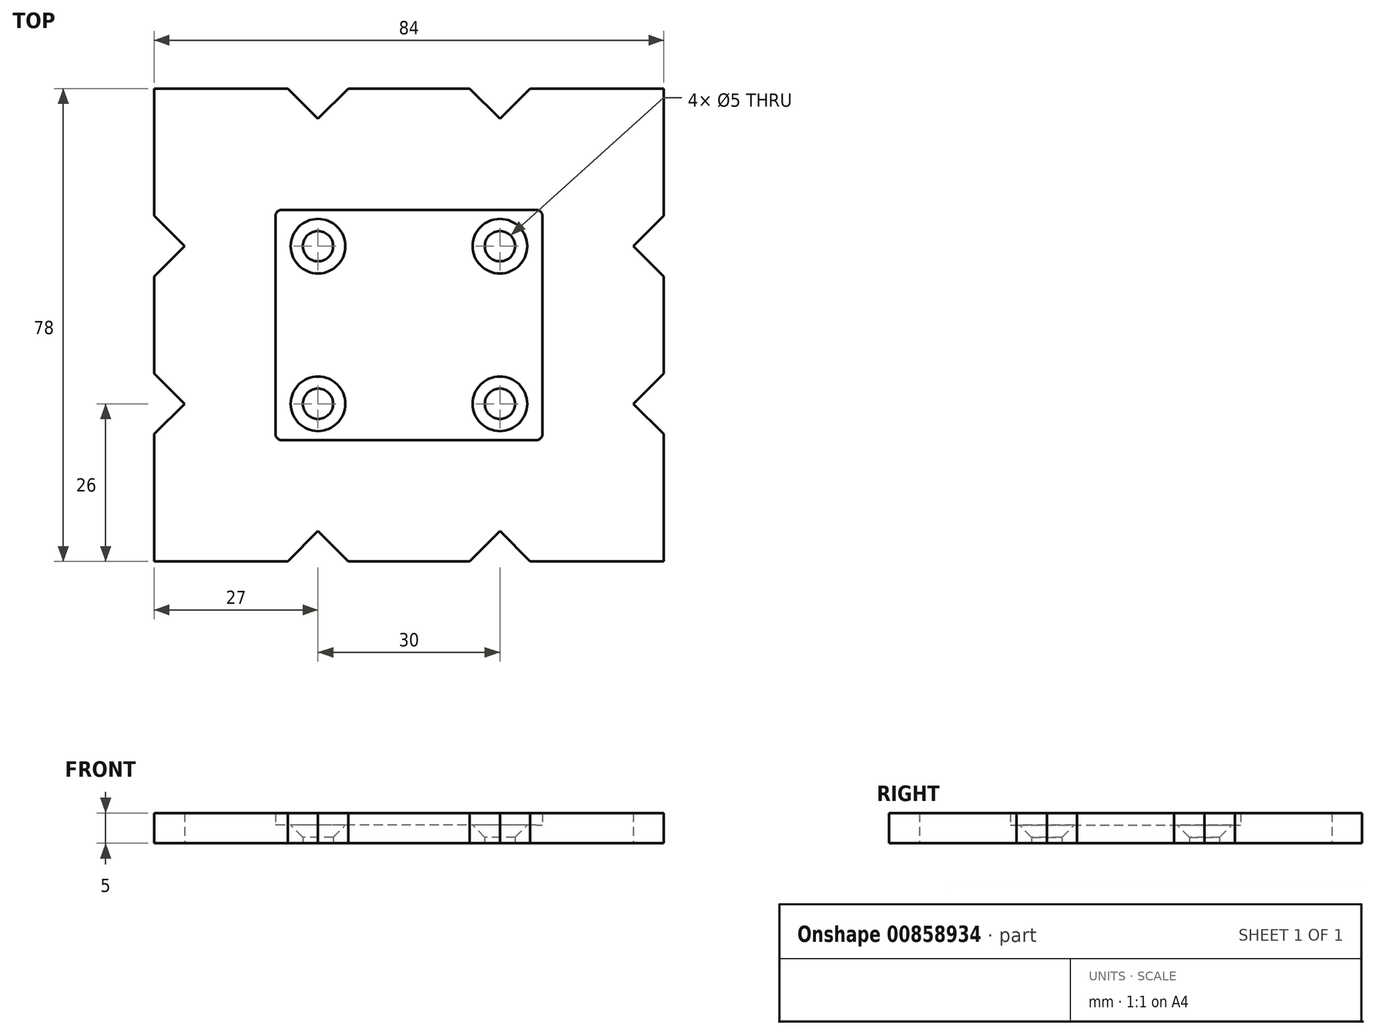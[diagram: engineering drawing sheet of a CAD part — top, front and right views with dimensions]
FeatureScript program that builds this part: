
annotation { "Feature Type Name" : "Feature", "Feature Type Description" : "" }
export const myFeature = defineFeature(function(context is Context, id is Id, definition is map)
    precondition{}
    {
        {
            var Q0;
            Q0=qCreatedBy(makeId("Top.planeOp"),FACE);
            var sketch = newSketch(context, id + "F0", { "sketchPlane" : qUnion([Q0])});
            skCircle(sketch, "E0", {"center": v(-15, 13) * mm, "radius": 2.5 * mm});
            skCircle(sketch, "E1", {"center": v(15, 13) * mm, "radius": 2.5 * mm});
            skCircle(sketch, "E2", {"center": v(-15, -13) * mm, "radius": 2.5 * mm});
            skCircle(sketch, "E3", {"center": v(15, -13) * mm, "radius": 2.5 * mm});
            skLineSegment(sketch, "E4.bottom", {"start": v(-22, 19) * mm, "end": v(22, 19) * mm});
            skLineSegment(sketch, "E4.top", {"start": v(-22, -19) * mm, "end": v(22, -19) * mm});
            skLineSegment(sketch, "E4.left", {"start": v(-22, 19) * mm, "end": v(-22, -19) * mm});
            skLineSegment(sketch, "E4.right", {"start": v(22, 19) * mm, "end": v(22, -19) * mm});
            skLineSegment(sketch, "E5.0", {"start": v(-42, -39) * mm, "end": v(42, -39) * mm});
            skLineSegment(sketch, "E5.1", {"start": v(-42, 39) * mm, "end": v(-42, -39) * mm});
            skLineSegment(sketch, "E5.2", {"start": v(-42, 39) * mm, "end": v(42, 39) * mm});
            skLineSegment(sketch, "E5.3", {"start": v(42, 39) * mm, "end": v(42, -39) * mm});
            skLineSegment(sketch, "E6", {"start": v(-15, 39) * mm, "end": v(-15, -39) * mm});
            skLineSegment(sketch, "E7", {"start": v(15, -39) * mm, "end": v(15, 39) * mm});
            skLineSegment(sketch, "E8", {"start": v(-20, -39) * mm, "end": v(-15, -34) * mm});
            skLineSegment(sketch, "E9", {"start": v(-15, -34) * mm, "end": v(-10, -39) * mm});
            skLineSegment(sketch, "E10", {"start": v(-10, -39) * mm, "end": v(-20, -39) * mm});
            skLineSegment(sketch, "E11.MirrorCS", {"start": v(15, -34) * mm, "end": v(10, -39) * mm});
            skLineSegment(sketch, "E12.MirrorCS", {"start": v(20, -39) * mm, "end": v(15, -34) * mm});
            skLineSegment(sketch, "E13.MirrorCS", {"start": v(10, -39) * mm, "end": v(20, -39) * mm});
            skLineSegment(sketch, "E14.MirrorCS", {"start": v(-20, 39) * mm, "end": v(-15, 34) * mm});
            skLineSegment(sketch, "E15.MirrorCS", {"start": v(-10, 39) * mm, "end": v(-20, 39) * mm});
            skLineSegment(sketch, "E16.MirrorCS", {"start": v(-15, 34) * mm, "end": v(-10, 39) * mm});
            skLineSegment(sketch, "E17.MirrorCS", {"start": v(15, 34) * mm, "end": v(10, 39) * mm});
            skLineSegment(sketch, "E18.MirrorCS", {"start": v(10, 39) * mm, "end": v(20, 39) * mm});
            skLineSegment(sketch, "E19.MirrorCS", {"start": v(20, 39) * mm, "end": v(15, 34) * mm});
            skLineSegment(sketch, "E20", {"start": v(42, -13) * mm, "end": v(-42, -13) * mm});
            skLineSegment(sketch, "E21", {"start": v(42, 13) * mm, "end": v(-42, 13) * mm});
            skLineSegment(sketch, "E22", {"start": v(42, -18) * mm, "end": v(37, -13) * mm});
            skLineSegment(sketch, "E23", {"start": v(37, -13) * mm, "end": v(42, -8) * mm});
            skLineSegment(sketch, "E24", {"start": v(42, -8) * mm, "end": v(42, -18) * mm});
            skLineSegment(sketch, "E25.MirrorCS", {"start": v(37, 13) * mm, "end": v(42, 8) * mm});
            skLineSegment(sketch, "E26.MirrorCS", {"start": v(42, -39) * mm, "end": v(42, 39) * mm});
            skLineSegment(sketch, "E27.MirrorCS", {"start": v(42, 18) * mm, "end": v(37, 13) * mm});
            skLineSegment(sketch, "E28.MirrorCS", {"start": v(-37, -13) * mm, "end": v(-42, -8) * mm});
            skLineSegment(sketch, "E29.MirrorCS", {"start": v(-42, -18) * mm, "end": v(-37, -13) * mm});
            skLineSegment(sketch, "E30.MirrorCS", {"start": v(-37, 13) * mm, "end": v(-42, 8) * mm});
            skLineSegment(sketch, "E31.MirrorCS", {"start": v(-42, 18) * mm, "end": v(-37, 13) * mm});
            skSolve(sketch);
        }
        {
            var Q0;
            {var subQ6=sQuery(id+"F0.wireOp",EDGE,"E28.MirrorCS");Q0=makeQuery(id+"F0.imprint","IMPRINT",FACE,{"disambiguationData":[TD([[makeQuery(id+"F0.imprint","IMPRINT",EDGE,{"derivedFrom":subQ6}),-1.0]])]});}
            var Q1;
            {var subQ0=sQuery(id+"F0.wireOp",EDGE,"E6");var subQ3=sQuery(id+"F0.wireOp",EDGE,"E0");var subQ4=makeQuery(id+"F0.imprint","INTERSECT",VERTEX,{"disambiguationData":[OD(1.0)],"derivedFrom":[subQ3,subQ0]});Q1=makeQuery(id+"F0.imprint","IMPRINT",FACE,{"disambiguationData":[TD([[makeQuery(id+"F0.imprint","IMPRINT",EDGE,{"disambiguationData":[TD([[subQ4,1.0]])],"derivedFrom":subQ3}),-1.0]])]});}
            var Q2;
            {var subQ4=sQuery(id+"F0.wireOp",EDGE,"E23");Q2=makeQuery(id+"F0.imprint","IMPRINT",FACE,{"disambiguationData":[TD([[makeQuery(id+"F0.imprint","IMPRINT",EDGE,{"derivedFrom":subQ4}),1.0]])]});}
            var Q3;
            {var subQ0=sQuery(id+"F0.wireOp",EDGE,"E7");var subQ1=sQuery(id+"F0.wireOp",EDGE,"E3");var subQ7=sQuery(id+"F0.wireOp",EDGE,"E20");var subQ9=makeQuery(id+"F0.imprint","INTERSECT",VERTEX,{"disambiguationData":[OD(1.0)],"derivedFrom":[subQ1,subQ7]});var subQ14=sQuery(id+"F0.wireOp",EDGE,"E1");var subQ15=makeQuery(id+"F0.imprint","INTERSECT",VERTEX,{"disambiguationData":[OD(0.0)],"derivedFrom":[subQ14,subQ0]});Q3=qUnion([makeQuery(id+"F0.imprint","IMPRINT",FACE,{"disambiguationData":[TD([[makeQuery(id+"F0.imprint","IMPRINT",EDGE,{"disambiguationData":[TD([[subQ15,1.0]])],"derivedFrom":subQ14}),-1.0]])]}),makeQuery(id+"F0.imprint","IMPRINT",FACE,{"disambiguationData":[TD([[makeQuery(id+"F0.imprint","IMPRINT",EDGE,{"disambiguationData":[TD([[subQ9,1.0]])],"derivedFrom":subQ1}),-1.0]])]})]);}
            var Q4;
            {var subQ0=sQuery(id+"F0.wireOp",EDGE,"E6");var subQ3=sQuery(id+"F0.wireOp",EDGE,"E2");var subQ7=sQuery(id+"F0.wireOp",EDGE,"E20");var subQ9=makeQuery(id+"F0.imprint","INTERSECT",VERTEX,{"disambiguationData":[OD(1.0)],"derivedFrom":[subQ3,subQ7]});var subQ14=sQuery(id+"F0.wireOp",EDGE,"E0");var subQ15=makeQuery(id+"F0.imprint","INTERSECT",VERTEX,{"disambiguationData":[OD(1.0)],"derivedFrom":[subQ14,subQ0]});Q4=qUnion([makeQuery(id+"F0.imprint","IMPRINT",FACE,{"disambiguationData":[TD([[makeQuery(id+"F0.imprint","IMPRINT",EDGE,{"disambiguationData":[TD([[subQ15,-1.0]])],"derivedFrom":subQ14}),-1.0]])]}),makeQuery(id+"F0.imprint","IMPRINT",FACE,{"disambiguationData":[TD([[makeQuery(id+"F0.imprint","IMPRINT",EDGE,{"disambiguationData":[TD([[subQ9,-1.0]])],"derivedFrom":subQ3}),-1.0]])]})]);}
            var Q5;
            {var subQ6=sQuery(id+"F0.wireOp",EDGE,"E16.MirrorCS");Q5=makeQuery(id+"F0.imprint","IMPRINT",FACE,{"disambiguationData":[TD([[makeQuery(id+"F0.imprint","IMPRINT",EDGE,{"derivedFrom":subQ6}),-1.0]])]});}
            var Q6;
            {var subQ3=sQuery(id+"F0.wireOp",EDGE,"E9");Q6=makeQuery(id+"F0.imprint","IMPRINT",FACE,{"disambiguationData":[TD([[makeQuery(id+"F0.imprint","IMPRINT",EDGE,{"derivedFrom":subQ3}),1.0]])]});}
            var Q7;
            {var subQ3=sQuery(id+"F0.wireOp",EDGE,"E8");Q7=makeQuery(id+"F0.imprint","IMPRINT",FACE,{"disambiguationData":[TD([[makeQuery(id+"F0.imprint","IMPRINT",EDGE,{"derivedFrom":subQ3}),1.0]])]});}
            var Q8;
            {var subQ3=sQuery(id+"F0.wireOp",EDGE,"E14.MirrorCS");Q8=makeQuery(id+"F0.imprint","IMPRINT",FACE,{"disambiguationData":[TD([[makeQuery(id+"F0.imprint","IMPRINT",EDGE,{"derivedFrom":subQ3}),-1.0]])]});}
            var Q9;
            {var subQ9=sQuery(id+"F0.wireOp",EDGE,"E19.MirrorCS");Q9=makeQuery(id+"F0.imprint","IMPRINT",FACE,{"disambiguationData":[TD([[makeQuery(id+"F0.imprint","IMPRINT",EDGE,{"derivedFrom":subQ9}),1.0]])]});}
            var Q10;
            {var subQ9=sQuery(id+"F0.wireOp",EDGE,"E12.MirrorCS");Q10=makeQuery(id+"F0.imprint","IMPRINT",FACE,{"disambiguationData":[TD([[makeQuery(id+"F0.imprint","IMPRINT",EDGE,{"derivedFrom":subQ9}),-1.0]])]});}
            var Q11;
            {var subQ9=sQuery(id+"F0.wireOp",EDGE,"E6");var subQ13=sQuery(id+"F0.wireOp",EDGE,"E0");var subQ14=makeQuery(id+"F0.imprint","INTERSECT",VERTEX,{"disambiguationData":[OD(0.0)],"derivedFrom":[subQ13,subQ9]});Q11=makeQuery(id+"F0.imprint","IMPRINT",FACE,{"disambiguationData":[TD([[makeQuery(id+"F0.imprint","IMPRINT",EDGE,{"disambiguationData":[TD([[subQ14,-1.0]])],"derivedFrom":subQ13}),-1.0]])]});}
            var Q12;
            {var subQ3=sQuery(id+"F0.wireOp",EDGE,"E2");var subQ9=sQuery(id+"F0.wireOp",EDGE,"E20");var subQ11=makeQuery(id+"F0.imprint","INTERSECT",VERTEX,{"disambiguationData":[OD(0.0)],"derivedFrom":[subQ3,subQ9]});Q12=makeQuery(id+"F0.imprint","IMPRINT",FACE,{"disambiguationData":[TD([[makeQuery(id+"F0.imprint","IMPRINT",EDGE,{"disambiguationData":[TD([[subQ11,1.0]])],"derivedFrom":subQ3}),-1.0]])]});}
            var Q13;
            {var subQ0=sQuery(id+"F0.wireOp",EDGE,"E6");var subQ1=sQuery(id+"F0.wireOp",EDGE,"E0");var subQ2=makeQuery(id+"F0.imprint","INTERSECT",VERTEX,{"disambiguationData":[OD(0.0)],"derivedFrom":[subQ1,subQ0]});Q13=makeQuery(id+"F0.imprint","IMPRINT",FACE,{"disambiguationData":[TD([[makeQuery(id+"F0.imprint","IMPRINT",EDGE,{"disambiguationData":[TD([[subQ2,1.0]])],"derivedFrom":subQ1}),-1.0]])]});}
            var Q14;
            {var subQ0=sQuery(id+"F0.wireOp",EDGE,"E21");var subQ8=sQuery(id+"F0.wireOp",EDGE,"E1");var subQ11=makeQuery(id+"F0.imprint","INTERSECT",VERTEX,{"disambiguationData":[OD(1.0)],"derivedFrom":[subQ8,subQ0]});Q14=makeQuery(id+"F0.imprint","IMPRINT",FACE,{"disambiguationData":[TD([[makeQuery(id+"F0.imprint","IMPRINT",EDGE,{"disambiguationData":[TD([[subQ11,1.0]])],"derivedFrom":subQ8}),-1.0]])]});}
            extrude(context, id + "F1", {"entities" : qUnion([Q0, Q1, Q2, Q3, Q4, Q5, Q6, Q7, Q8, Q9, Q10, Q11, Q12, Q13, Q14]), "depth" : 3 * mm, "offsetDistance" : 25 * mm});
        }
        {
            var Q0;
            Q0=makeQuery(id+"F1.opExtrude","CAP_EDGE",EDGE,{"disambiguationData":[OSD([sQuery(id+"F0.wireOp",EDGE,"E2")])],"isStart":false});
            var Q1;
            Q1=makeQuery(id+"F1.opExtrude","CAP_EDGE",EDGE,{"disambiguationData":[OSD([sQuery(id+"F0.wireOp",EDGE,"E0")])],"isStart":false});
            var Q2;
            Q2=makeQuery(id+"F1.opExtrude","CAP_EDGE",EDGE,{"disambiguationData":[OSD([sQuery(id+"F0.wireOp",EDGE,"E1")])],"isStart":false});
            var Q3;
            Q3=makeQuery(id+"F1.opExtrude","CAP_EDGE",EDGE,{"disambiguationData":[OSD([sQuery(id+"F0.wireOp",EDGE,"E3")])],"isStart":false});
            chamfer(context, id + "F2", {"entities" : qUnion([Q0, Q1, Q2, Q3]), "width" : 2 * mm, "tangentPropagation" : true});
        }
        {
            var Q0;
            Q0=makeQuery(id+"F1.opExtrude","CAP_EDGE",EDGE,{"disambiguationData":[OSD([sQuery(id+"F0.wireOp",EDGE,"E22")])],"isStart":false});
            var Q1;
            Q1=makeQuery(id+"F1.opExtrude","CAP_EDGE",EDGE,{"disambiguationData":[OSD([sQuery(id+"F0.wireOp",EDGE,"E23")])],"isStart":false});
            var Q2;
            Q2=makeQuery(id+"F1.opExtrude","CAP_EDGE",EDGE,{"disambiguationData":[OSD([sQuery(id+"F0.wireOp",EDGE,"E25.MirrorCS")])],"isStart":false});
            var Q3;
            Q3=makeQuery(id+"F1.opExtrude","CAP_EDGE",EDGE,{"disambiguationData":[OSD([sQuery(id+"F0.wireOp",EDGE,"E27.MirrorCS")])],"isStart":false});
            var Q4;
            Q4=makeQuery(id+"F1.opExtrude","CAP_EDGE",EDGE,{"disambiguationData":[OSD([sQuery(id+"F0.wireOp",EDGE,"E19.MirrorCS")])],"isStart":false});
            var Q5;
            Q5=makeQuery(id+"F1.opExtrude","CAP_EDGE",EDGE,{"disambiguationData":[OSD([sQuery(id+"F0.wireOp",EDGE,"E17.MirrorCS")])],"isStart":false});
            var Q6;
            Q6=makeQuery(id+"F1.opExtrude","CAP_EDGE",EDGE,{"disambiguationData":[OSD([sQuery(id+"F0.wireOp",EDGE,"E16.MirrorCS")])],"isStart":false});
            var Q7;
            Q7=makeQuery(id+"F1.opExtrude","CAP_EDGE",EDGE,{"disambiguationData":[OSD([sQuery(id+"F0.wireOp",EDGE,"E14.MirrorCS")])],"isStart":false});
            var Q8;
            Q8=makeQuery(id+"F1.opExtrude","CAP_EDGE",EDGE,{"disambiguationData":[OSD([sQuery(id+"F0.wireOp",EDGE,"E31.MirrorCS")])],"isStart":false});
            var Q9;
            Q9=makeQuery(id+"F1.opExtrude","CAP_EDGE",EDGE,{"disambiguationData":[OSD([sQuery(id+"F0.wireOp",EDGE,"E30.MirrorCS")])],"isStart":false});
            var Q10;
            Q10=makeQuery(id+"F1.opExtrude","CAP_EDGE",EDGE,{"disambiguationData":[OSD([sQuery(id+"F0.wireOp",EDGE,"E28.MirrorCS")])],"isStart":false});
            var Q11;
            Q11=makeQuery(id+"F1.opExtrude","CAP_EDGE",EDGE,{"disambiguationData":[OSD([sQuery(id+"F0.wireOp",EDGE,"E29.MirrorCS")])],"isStart":false});
            var Q12;
            Q12=makeQuery(id+"F1.opExtrude","CAP_EDGE",EDGE,{"disambiguationData":[OSD([sQuery(id+"F0.wireOp",EDGE,"E8")])],"isStart":false});
            var Q13;
            Q13=makeQuery(id+"F1.opExtrude","CAP_EDGE",EDGE,{"disambiguationData":[OSD([sQuery(id+"F0.wireOp",EDGE,"E9")])],"isStart":false});
            var Q14;
            Q14=makeQuery(id+"F1.opExtrude","CAP_EDGE",EDGE,{"disambiguationData":[OSD([sQuery(id+"F0.wireOp",EDGE,"E11.MirrorCS")])],"isStart":false});
            var Q15;
            Q15=makeQuery(id+"F1.opExtrude","CAP_EDGE",EDGE,{"disambiguationData":[OSD([sQuery(id+"F0.wireOp",EDGE,"E12.MirrorCS")])],"isStart":false});
            chamfer(context, id + "F3", {"entities" : qUnion([Q0, Q1, Q2, Q3, Q4, Q5, Q6, Q7, Q8, Q9, Q10, Q11, Q12, Q13, Q14, Q15]), "width" : 3 * mm, "tangentPropagation" : true});
        }
        {
            var Q0;
            {var subQ3=sQuery(id+"F0.wireOp",EDGE,"E14.MirrorCS");Q0=makeQuery(id+"F0.imprint","IMPRINT",FACE,{"disambiguationData":[TD([[makeQuery(id+"F0.imprint","IMPRINT",EDGE,{"derivedFrom":subQ3}),-1.0]])]});}
            var Q1;
            {var subQ6=sQuery(id+"F0.wireOp",EDGE,"E28.MirrorCS");Q1=makeQuery(id+"F0.imprint","IMPRINT",FACE,{"disambiguationData":[TD([[makeQuery(id+"F0.imprint","IMPRINT",EDGE,{"derivedFrom":subQ6}),-1.0]])]});}
            var Q2;
            {var subQ3=sQuery(id+"F0.wireOp",EDGE,"E8");Q2=makeQuery(id+"F0.imprint","IMPRINT",FACE,{"disambiguationData":[TD([[makeQuery(id+"F0.imprint","IMPRINT",EDGE,{"derivedFrom":subQ3}),1.0]])]});}
            var Q3;
            {var subQ3=sQuery(id+"F0.wireOp",EDGE,"E9");Q3=makeQuery(id+"F0.imprint","IMPRINT",FACE,{"disambiguationData":[TD([[makeQuery(id+"F0.imprint","IMPRINT",EDGE,{"derivedFrom":subQ3}),1.0]])]});}
            var Q4;
            {var subQ9=sQuery(id+"F0.wireOp",EDGE,"E12.MirrorCS");Q4=makeQuery(id+"F0.imprint","IMPRINT",FACE,{"disambiguationData":[TD([[makeQuery(id+"F0.imprint","IMPRINT",EDGE,{"derivedFrom":subQ9}),-1.0]])]});}
            var Q5;
            {var subQ4=sQuery(id+"F0.wireOp",EDGE,"E23");Q5=makeQuery(id+"F0.imprint","IMPRINT",FACE,{"disambiguationData":[TD([[makeQuery(id+"F0.imprint","IMPRINT",EDGE,{"derivedFrom":subQ4}),1.0]])]});}
            var Q6;
            {var subQ9=sQuery(id+"F0.wireOp",EDGE,"E19.MirrorCS");Q6=makeQuery(id+"F0.imprint","IMPRINT",FACE,{"disambiguationData":[TD([[makeQuery(id+"F0.imprint","IMPRINT",EDGE,{"derivedFrom":subQ9}),1.0]])]});}
            var Q7;
            {var subQ6=sQuery(id+"F0.wireOp",EDGE,"E16.MirrorCS");Q7=makeQuery(id+"F0.imprint","IMPRINT",FACE,{"disambiguationData":[TD([[makeQuery(id+"F0.imprint","IMPRINT",EDGE,{"derivedFrom":subQ6}),-1.0]])]});}
            extrude(context, id + "F4", {"entities" : qUnion([Q0, Q1, Q2, Q3, Q4, Q5, Q6, Q7]), "operationType" : NewBodyOperationType.ADD, "depth" : 5 * mm, "offsetDistance" : 25 * mm});
        }
        {
            var Q0;
            Q0=makeQuery(id+"F4.opExtrude","SWEPT_EDGE",EDGE,{"disambiguationData":[OSD([sQuery(id+"F0.wireOp",EDGE,"E4.bottom"),sQuery(id+"F0.wireOp",EDGE,"E4.left")])]});
            var Q1;
            Q1=makeQuery(id+"F4.opExtrude","SWEPT_EDGE",EDGE,{"disambiguationData":[OSD([sQuery(id+"F0.wireOp",EDGE,"E4.top"),sQuery(id+"F0.wireOp",EDGE,"E4.left")])]});
            var Q2;
            Q2=makeQuery(id+"F4.opExtrude","SWEPT_EDGE",EDGE,{"disambiguationData":[OSD([sQuery(id+"F0.wireOp",EDGE,"E4.bottom"),sQuery(id+"F0.wireOp",EDGE,"E4.right")])]});
            var Q3;
            Q3=makeQuery(id+"F4.opExtrude","SWEPT_EDGE",EDGE,{"disambiguationData":[OSD([sQuery(id+"F0.wireOp",EDGE,"E4.top"),sQuery(id+"F0.wireOp",EDGE,"E4.right")])]});
            fillet(context, id + "F5", {"entities" : qUnion([Q0, Q1, Q2, Q3]), "radius" : 1 * mm, "tangentPropagation" : true, "allowEdgeOverflow" : false});
        }
    });
